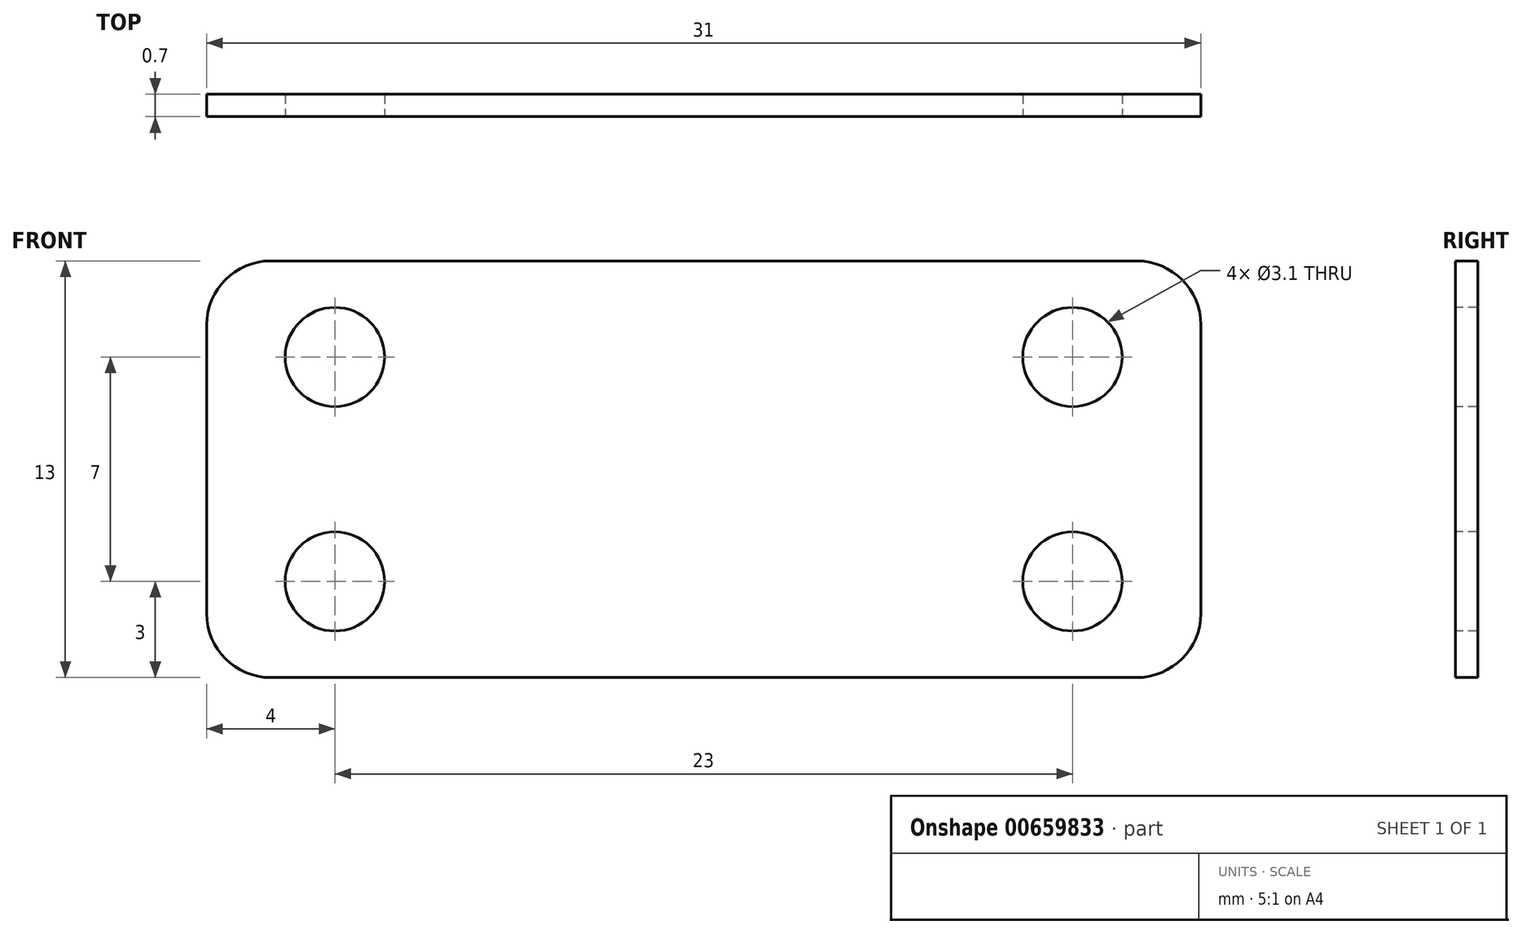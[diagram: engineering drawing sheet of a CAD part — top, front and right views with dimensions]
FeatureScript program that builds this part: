
annotation { "Feature Type Name" : "Feature", "Feature Type Description" : "" }
export const myFeature = defineFeature(function(context is Context, id is Id, definition is map)
    precondition{}
    {
        {
            var Q0;
            Q0=qCreatedBy(makeId("Front.planeOp"),FACE);
            var sketch = newSketch(context, id + "F0", { "sketchPlane" : qUnion([Q0])});
            skLineSegment(sketch, "E0.bottom", {"start": v(0, 0) * mm, "end": v(31, 0) * mm});
            skLineSegment(sketch, "E0.top", {"start": v(0, 13) * mm, "end": v(31, 13) * mm});
            skLineSegment(sketch, "E0.left", {"start": v(0, 0) * mm, "end": v(0, 13) * mm});
            skLineSegment(sketch, "E0.right", {"start": v(31, 0) * mm, "end": v(31, 13) * mm});
            skSolve(sketch);
        }
        {
            var Q0;
            Q0=qSketchRegion(id+"F0",true);
            extrude(context, id + "F1", {"entities" : qUnion([Q0]), "depth" : 0.7 * mm, "offsetDistance" : 25 * mm});
        }
        {
            var Q0;
            Q0=makeQuery(id+"F1.opExtrude","CAP_FACE",FACE,{"disambiguationData":[OSD([sQuery(id+"F0.wireOp",EDGE,"E0.bottom"),sQuery(id+"F0.wireOp",EDGE,"E0.top"),sQuery(id+"F0.wireOp",EDGE,"E0.left"),sQuery(id+"F0.wireOp",EDGE,"E0.right"),sQuery(id+"F0.wireOp",EDGE,"kQiuNbPG-d7aO-r9iV-VTQa-4taDSfapuuNw.bottom"),sQuery(id+"F0.wireOp",EDGE,"kQiuNbPG-d7aO-r9iV-VTQa-4taDSfapuuNw.top"),sQuery(id+"F0.wireOp",EDGE,"kQiuNbPG-d7aO-r9iV-VTQa-4taDSfapuuNw.left"),sQuery(id+"F0.wireOp",EDGE,"kQiuNbPG-d7aO-r9iV-VTQa-4taDSfapuuNw.right")])],"isStart":false});
            var sketch = newSketch(context, id + "F2", { "sketchPlane" : qUnion([Q0])});
            skCircle(sketch, "E1", {"center": v(4, 10) * mm, "radius": 1.55 * mm});
            skCircle(sketch, "E2.0.1.0", {"center": v(4, 3) * mm, "radius": 1.55 * mm});
            skCircle(sketch, "E2.1.0.0", {"center": v(27, 10) * mm, "radius": 1.55 * mm});
            skCircle(sketch, "E2.1.1.0", {"center": v(27, 3) * mm, "radius": 1.55 * mm});
            skLineSegment(sketch, "E2.direction1", {"start": v(4, 10) * mm, "end": v(27, 10) * mm, "construction": true});
            skLineSegment(sketch, "E2.direction2", {"start": v(4, 10) * mm, "end": v(4, 3) * mm, "construction": true});
            skSolve(sketch);
        }
        {
            var Q0;
            Q0=qSketchRegion(id+"F2",true);
            extrude(context, id + "F3", {"entities" : qUnion([Q0]), "operationType" : NewBodyOperationType.REMOVE, "oppositeDirection" : true, "depth" : 25 * mm, "offsetDistance" : 25 * mm});
        }
        {
            var Q0;
            Q0=makeQuery(id+"F1.opExtrude","SWEPT_EDGE",EDGE,{"disambiguationData":[OSD([sQuery(id+"F0.wireOp",EDGE,"E0.top"),sQuery(id+"F0.wireOp",EDGE,"E0.right")])]});
            var Q1;
            Q1=makeQuery(id+"F1.opExtrude","SWEPT_EDGE",EDGE,{"disambiguationData":[OSD([sQuery(id+"F0.wireOp",EDGE,"E0.bottom"),sQuery(id+"F0.wireOp",EDGE,"E0.right")])]});
            var Q2;
            Q2=makeQuery(id+"F1.opExtrude","SWEPT_EDGE",EDGE,{"disambiguationData":[OSD([sQuery(id+"F0.wireOp",EDGE,"E0.bottom"),sQuery(id+"F0.wireOp",EDGE,"E0.left")])]});
            var Q3;
            Q3=makeQuery(id+"F1.opExtrude","SWEPT_EDGE",EDGE,{"disambiguationData":[OSD([sQuery(id+"F0.wireOp",EDGE,"E0.top"),sQuery(id+"F0.wireOp",EDGE,"E0.left")])]});
            fillet(context, id + "F4", {"entities" : qUnion([Q0, Q1, Q2, Q3]), "radius" : 2 * mm, "tangentPropagation" : true, "allowEdgeOverflow" : false});
        }
    });
